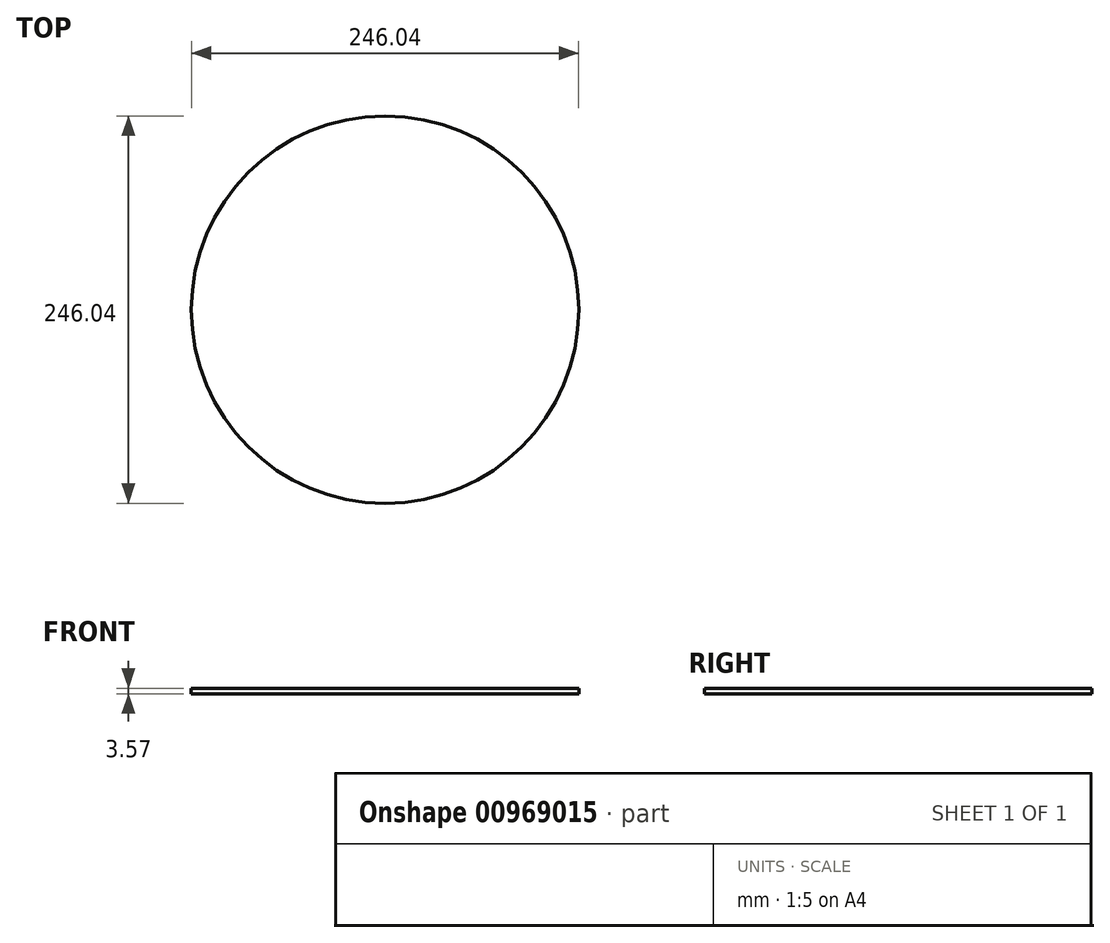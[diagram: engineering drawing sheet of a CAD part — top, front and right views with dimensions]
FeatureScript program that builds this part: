
annotation { "Feature Type Name" : "Feature", "Feature Type Description" : "" }
export const myFeature = defineFeature(function(context is Context, id is Id, definition is map)
    precondition{}
    {
        {
            var Q0;
            Q0=qCreatedBy(makeId("Top.planeOp"),FACE);
            var sketch = newSketch(context, id + "F0", { "sketchPlane" : qUnion([Q0])});
            skCircle(sketch, "E0", {"center": v(0, 0) * mm, "radius": 123.02 * mm});
            skSolve(sketch);
        }
        {
            var Q0;
            Q0 = qSketchRegion(id + "F0", true);
            extrude(context, id + "F1", {"entities" : qUnion([Q0]), "depth" : 3.57 * mm, "offsetDistance" : 25.4 * mm});
        }
    });
